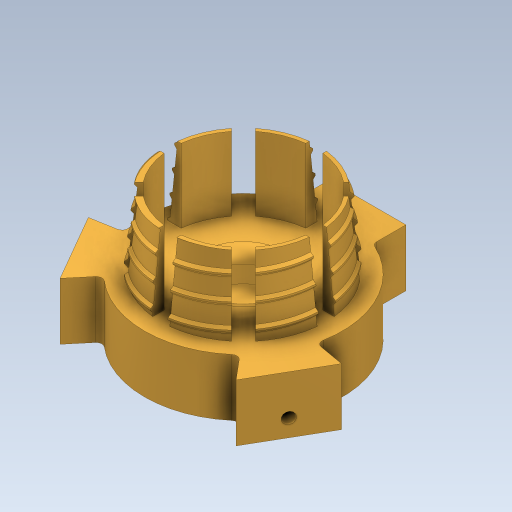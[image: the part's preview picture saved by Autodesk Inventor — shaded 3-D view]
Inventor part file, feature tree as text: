
AUTODESK INVENTOR PART (.ipt)
format: ipt  version: 2023 (Build 270158000, 158)  size: 2,155,520 bytes
history: native  units: mm
features: sketch x8, extrude x4, hole x3, helix x2, fillet x2, draft x1, direct_edit x1, pattern_circular x1, other x1
ambient origin geometry x8: Origin, YZ Plane, XZ Plane, XY Plane, X Axis, Y Axis, Z Axis, Center Point
bodies: Solid1 (feature_tree)
feature tree (23):
  extrude  "Extrusion1"  Depth=26.5mm
  draft  "FaceDraft1"
  sketch  "Sketch2"  dims[d34=0.0mm d35=0.0mm d56=8.726646mm]
  helix  "Coil3"  [1 undecoded]
  helix  "Coil4"  [1 undecoded]
  direct_edit  "Direct Edit2"
  extrude  "Extrusion2"  Depth=8.726646mm
  extrude  "Extrusion13"  TaperAngle=90.0deg  [1 undecoded]
  extrude  "Extrusion14"  Depth=34.58632mm
  fillet  "Fillet10"  [1 undecoded]
  hole  "Hole2"  [1 undecoded]
  pattern_circular  "Circular Pattern2"  [2 undecoded]
  hole  "Hole3"  [1 undecoded]
  hole  "Hole4"  [1 undecoded]
  fillet  "Fillet11"  Radius=3.0mm
  sketch  "Sketch1"  dims[d0=25.0mm d1=26.5mm d2=12.875mm d3=0.0mm d4=1.047198mm]
  sketch  "Sketch3"  dims[d62=4.0mm d63=13.0mm d64=10.0mm d65=1.047198mm]
  sketch  "Sketch10"  dims[d66=90.0deg d67=90.0deg d68=0.0mm d69=0.0mm d70=4.0mm d71=3.0mm d72=10.0mm d73=-1.047198mm d74=90.0deg d75=90.0deg d76=0.0mm d77=0.0mm]
  sketch  "Sketch11"  dims[d79=-0.127mm d145=34.58632mm d150=120.0deg]
  sketch  "Sketch12"  dims[d151=120.0deg d152=13.5mm]
  sketch  "Sketch13"  dims[d153=21.6866mm]
  sketch  "Sketch14"  dims[d154=12.217305mm d155=21.6866mm d156=13.5mm d157=10.0mm d158=0.0mm d159=3.0mm d160=80.0mm d162=360.0deg d164=0.0mm d165=0.0mm d166=1.0mm d167=2.0mm d168=7.0mm d169=2.0mm d170=6.0mm d171=4.0mm d172=2.0mm d173=90.0deg d174=5.0mm d175=0.0mm d176=20.0mm d177=120.0deg d179=5.3mm d180=6.0mm d181=4.0mm d182=2.0mm d183=90.0deg d184=5.0mm d185=0.0mm d186=10.0mm d187=6.0mm d188=4.0mm d189=2.0mm d190=90.0deg d191=7.0mm d192=0.0mm d193=2.0mm d109=0.5mm d110=0.872665mm d111=0.5mm d112=0.872665mm]
  other  "Size2"
note: 9 required parameter values undecoded (feature->parameter linkage not recoverable at this tier; creation-order binding heuristic only, values carry confidence <= 0.55)
